annotation { "Feature Type Name" : "Feature", "Feature Type Description" : "" }
export const myFeature = defineFeature(function(context is Context, id is Id, definition is map)
    precondition{}
    {
        {
            var Q0;
            Q0=qCreatedBy(makeId("Front.planeOp"),FACE);
            var sketch = newSketch(context, id + "F0", { "sketchPlane" : qUnion([Q0])});
            skText(sketch, "E0", { "text": "Flemming Jensen", "fontName": "OpenSans-Regular.ttf"});
            skPoint(sketch, "E1", {"position": v(0.21, 0) * mm});
            skLineSegment(sketch, "E2.bottom", {"start": v(-55.31, 27.19) * mm, "end": v(54.69, 27.19) * mm});
            skLineSegment(sketch, "E2.top", {"start": v(-55.31, -7.81) * mm, "end": v(54.69, -7.81) * mm});
            skLineSegment(sketch, "E2.left", {"start": v(-55.31, 27.19) * mm, "end": v(-55.31, -7.81) * mm});
            skLineSegment(sketch, "E2.right", {"start": v(54.69, 27.19) * mm, "end": v(54.69, -7.81) * mm});
            skArc(sketch, "E3", {"start": v(38.13, 27.19) * mm, "mid": v(0, 65.31) * mm, "end": v(-38.13, 27.19) * mm});
            skCircle(sketch, "E4", {"center": v(0, 45.63) * mm, "radius": 4 * mm});
            const initialGuessF0  = {"E0": [-0.04979, 0, 1, 0, 0.00906]};
            skSetInitialGuess(sketch, initialGuessF0);
            skSolve(sketch);
        }
        {
            var Q0;
            Q0=makeQuery(id+"F0.imprint","IMPRINT",FACE,{"disambiguationData":[TD([[makeQuery(id+"F0.imprint","IMPRINT",EDGE,{"derivedFrom":sQuery(id+"F0.wireOp",EDGE,"E0.sketch_text.stroke-0")}),1.0]])]});
            var Q1;
            {var subQ0=sQuery(id+"F0.wireOp",EDGE,"E3");Q1=makeQuery(id+"F0.imprint","IMPRINT",FACE,{"disambiguationData":[TD([[makeQuery(id+"F0.imprint","IMPRINT",EDGE,{"derivedFrom":subQ0}),1.0]])]});}
            extrude(context, id + "F1", {"entities" : qUnion([Q0, Q1]), "depth" : 3 * mm});
        }
    });